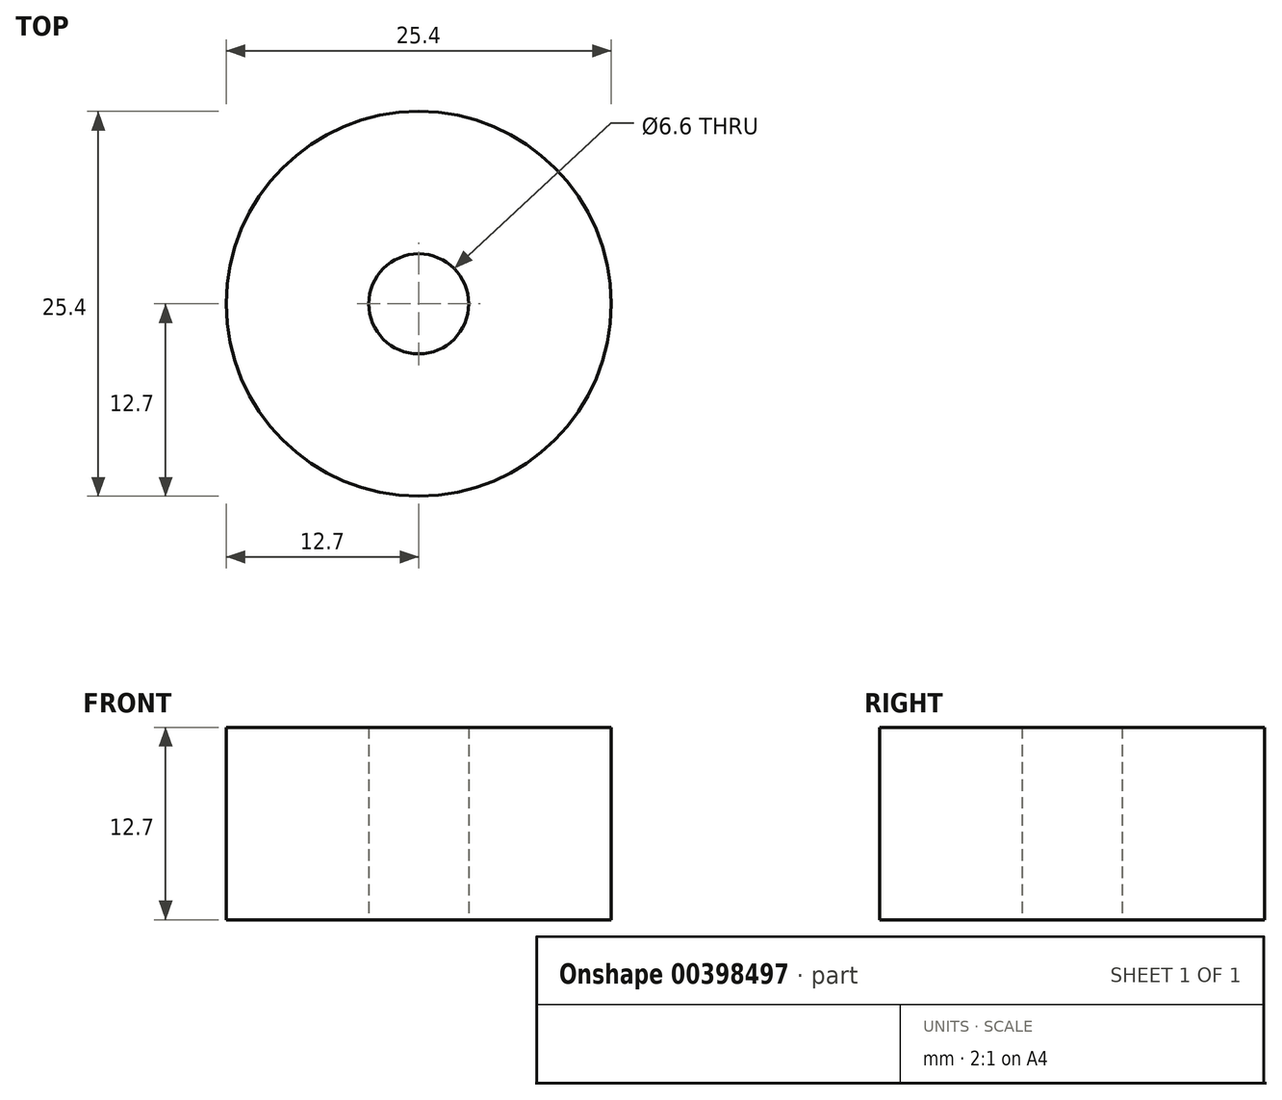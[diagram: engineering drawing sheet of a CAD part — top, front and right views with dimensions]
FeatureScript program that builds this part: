
annotation { "Feature Type Name" : "Feature", "Feature Type Description" : "" }
export const myFeature = defineFeature(function(context is Context, id is Id, definition is map)
    precondition{}
    {
        {
            var Q0;
            Q0=qCreatedBy(makeId("Top.planeOp"),FACE);
            var sketch = newSketch(context, id + "F0", { "sketchPlane" : qUnion([Q0])});
            skCircle(sketch, "E0", {"center": v(0, 0) * mm, "radius": 12.7 * mm});
            skPoint(sketch, "E1.orphan", {"position": v(0, 12.7) * mm});
            skCircle(sketch, "E2", {"center": v(0, 0) * mm, "radius": 3.3 * mm});
            skSolve(sketch);
        }
        {
            var Q0;
            Q0 = qSketchRegion(id + "F0", true);
            extrude(context, id + "F1", {"entities" : qUnion([Q0]), "depth" : 12.7 * mm});
        }
        {
            var Q0;
            Q0=makeQuery(id+"F1.opExtrude","CAP_FACE",FACE,{"disambiguationData":[OSD([sQuery(id+"F0.wireOp",EDGE,"E0"),sQuery(id+"F0.wireOp",EDGE,"E2")])],"isStart":false});
            var sketch = newSketch(context, id + "F2", { "sketchPlane" : qUnion([Q0])});
            skLineSegment(sketch, "E3", {"start": v(0, 12.7) * mm, "end": v(0, 9.9) * mm});
            skCircle(sketch, "E4", {"center": v(0, 9.9) * mm, "radius": 1.27 * mm});
            skCircle(sketch, "E5.1.0", {"center": v(-7, 7) * mm, "radius": 1.27 * mm});
            skCircle(sketch, "E5.2.0", {"center": v(-9.9, 0) * mm, "radius": 1.27 * mm});
            skCircle(sketch, "E5.3.0", {"center": v(-7, -7) * mm, "radius": 1.27 * mm});
            skCircle(sketch, "E5.4.0", {"center": v(0, -9.9) * mm, "radius": 1.27 * mm});
            skCircle(sketch, "E5.5.0", {"center": v(7, -7) * mm, "radius": 1.27 * mm});
            skCircle(sketch, "E5.6.0", {"center": v(9.9, 0) * mm, "radius": 1.27 * mm});
            skCircle(sketch, "E5.7.0", {"center": v(7, 7) * mm, "radius": 1.27 * mm});
            skPoint(sketch, "E5.center", {"position": v(0, 0) * mm});
            skSolve(sketch);
        }
        {
            var Q0;
            Q0=sQuery(id+"F2.wireOp",EDGE,"E5.1.0");
            var Q1;
            Q1=sQuery(id+"F2.wireOp",EDGE,"E4");
            var Q2;
            Q2=sQuery(id+"F2.wireOp",EDGE,"E5.7.0");
            var Q3;
            Q3=sQuery(id+"F2.wireOp",EDGE,"E5.6.0");
            var Q4;
            Q4=sQuery(id+"F2.wireOp",EDGE,"E5.5.0");
            var Q5;
            Q5=sQuery(id+"F2.wireOp",EDGE,"E5.4.0");
            var Q6;
            Q6=sQuery(id+"F2.wireOp",EDGE,"E5.3.0");
            var Q7;
            Q7=sQuery(id+"F2.wireOp",EDGE,"E5.2.0");
            extrude(context, id + "F3", {"bodyType" : ToolBodyType.SURFACE, "surfaceEntities" : qUnion([Q0, Q1, Q2, Q3, Q4, Q5, Q6, Q7]), "depth" : 12.7 * mm});
        }
    });
